# Revit family: External block R125_R335_3R1A
name_source: partatom
category: Оборудование
units: mm (PartAtom-declared; Revit-internal decimal feet)

## family parameters
Всегда вертикально = Да
Классификация = Нет
На основе рабочей плоскости = Нет
Общий = Нет
При загрузке вырезать с полостями = Нет
Размер круглого соединителя = Использовать диаметр
Тип детали = Нормальный
Точка принадлежности помещению = Нет

## types (9) — shared parameters
00_20_Manufacturer = BLAUBERG
00_20_Name = External block
Casing Material = Steel, white, mat
Electric = Нет
Grid Material = Mesh, steel, painted,  white
Load Classification = HVAC
Maintenance zone material = <По категории>
Maximum Air Flow = 0.0 л/с
Pressure_Static_Air = 0.0 Па
d = 10 мм
rn = 10 мм
Изготовитель = BLAUBERG
zero-valued in all types: Отметка по умолчанию

## per-type parameters (varying)
| type | A | B | C | Cp | Cv | D | Dv | E | Height | Lb | Length | Lv | Power | Weight | Width | d1 | h | wn |
| BLHV-R125-O/3R1A | 975 мм | 400 мм | 1335 мм | 568 мм | 334 мм | 586 мм | 518 мм | 370 мм | 1335 мм | 925 мм | 975 мм | 154 мм | 3260 Вт | 86.60 кг | 400 мм | 16 мм | 1315 мм | 268 мм |
| BLHV-R160-O/3R1A | 975 мм | 400 мм | 1335 мм | 568 мм | 334 мм | 586 мм | 518 мм | 370 мм | 1335 мм | 925 мм | 975 мм | 154 мм | 4610 Вт | 90.10 кг | 400 мм | 16 мм | 1315 мм | 268 мм |
| BLHV-R140-O/3R1A | 975 мм | 400 мм | 1335 мм | 568 мм | 334 мм | 586 мм | 518 мм | 370 мм | 1335 мм | 925 мм | 975 мм | 154 мм | 3970 Вт | 86.60 кг | 400 мм | 16 мм | 1315 мм | 268 мм |
| BLHV-R180-O/3R1A | 975 мм | 400 мм | 1335 мм | 568 мм | 334 мм | 586 мм | 518 мм | 370 мм | 1335 мм | 925 мм | 975 мм | 154 мм | 5020 Вт | 94.70 кг | 400 мм | 19 мм | 1315 мм | 268 мм |
| BLHV-R200-O/3R1A | 1015 мм | 450 мм | 1430 мм | 615 мм | 358 мм | 636 мм | 565 мм | 417 мм | 1430 мм | 965 мм | 1015 мм | 150 мм | 5350 Вт | 112.70 кг | 450 мм | 19 мм | 1410 мм | 293 мм |
| BLHV-R224-O/3R1A | 1015 мм | 450 мм | 1430 мм | 615 мм | 358 мм | 636 мм | 565 мм | 417 мм | 1430 мм | 965 мм | 1015 мм | 150 мм | 5620 Вт | 112.70 кг | 450 мм | 19 мм | 1410 мм | 293 мм |
| BLHV-R260-O/3R1A | 1278 мм | 450 мм | 1703 мм | 752 мм | 426 мм | 636 мм | 702 мм | 560 мм | 1703 мм | 1228 мм | 1278 мм | 213 мм | 6770 Вт | 142.00 кг | 450 мм | 22 мм | 1683 мм | 293 мм |
| BLHV-R280-O/3R1A | 1278 мм | 450 мм | 1703 мм | 752 мм | 426 мм | 636 мм | 702 мм | 560 мм | 1703 мм | 1228 мм | 1278 мм | 213 мм | 8180 Вт | 154.00 кг | 450 мм | 22 мм | 1683 мм | 293 мм |
| BLHV-R335-O/3R1A | 1278 мм | 450 мм | 1703 мм | 752 мм | 426 мм | 636 мм | 702 мм | 560 мм | 1703 мм | 1228 мм | 1278 мм | 213 мм | 8990 Вт | 154.00 кг | 450 мм | 22 мм | 1683 мм | 293 мм |

note: column(s) folded — value = type name in every type: 00_20_Type
